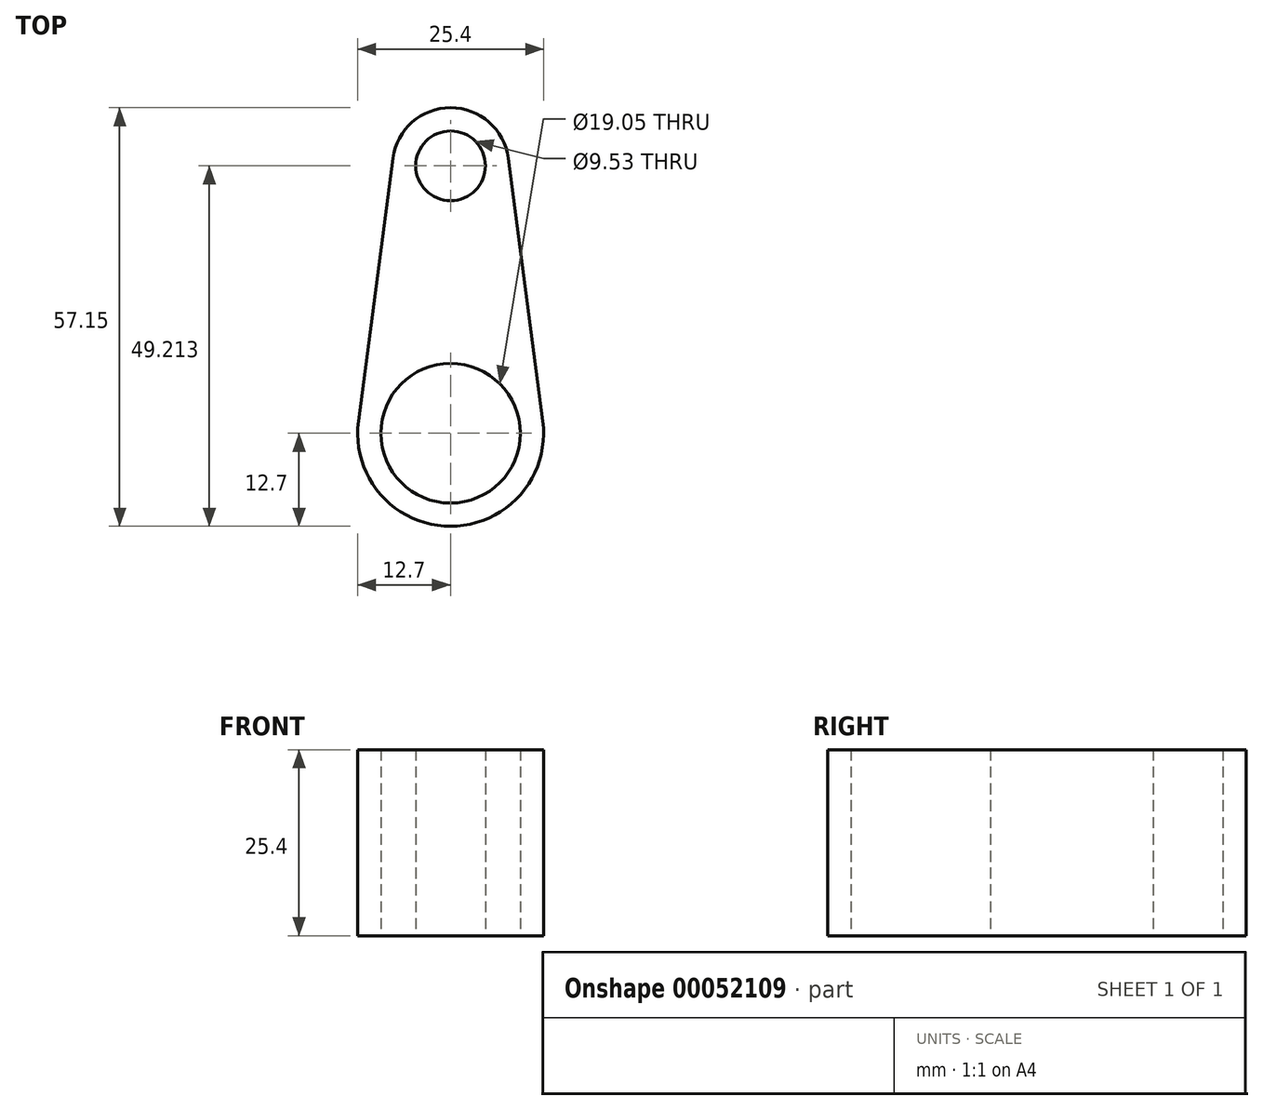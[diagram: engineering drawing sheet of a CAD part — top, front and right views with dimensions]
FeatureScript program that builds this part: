
annotation { "Feature Type Name" : "Feature", "Feature Type Description" : "" }
export const myFeature = defineFeature(function(context is Context, id is Id, definition is map)
    precondition{}
    {
        {
            var Q0;
            Q0=qCreatedBy(makeId("Top.planeOp"),FACE);
            var sketch = newSketch(context, id + "F0", { "sketchPlane" : qUnion([Q0])});
            skCircle(sketch, "E0", {"center": v(0, 0) * mm, "radius": 12.7 * mm});
            skCircle(sketch, "E1", {"center": v(0, 0) * mm, "radius": 9.53 * mm});
            skCircle(sketch, "E2", {"center": v(0, 36.51) * mm, "radius": 4.76 * mm});
            skCircle(sketch, "E3", {"center": v(0, 36.51) * mm, "radius": 7.94 * mm});
            skLineSegment(sketch, "E4", {"start": v(-12.6, 1.66) * mm, "end": v(-7.87, 37.55) * mm});
            skLineSegment(sketch, "E5", {"start": v(12.6, 1.66) * mm, "end": v(7.87, 37.55) * mm});
            skSolve(sketch);
        }
        {
            var Q0;
            Q0 = qSketchRegion(id + "F0", true);
            extrude(context, id + "F1", {"entities" : qUnion([Q0]), "depth" : 25.4 * mm});
        }
    });
